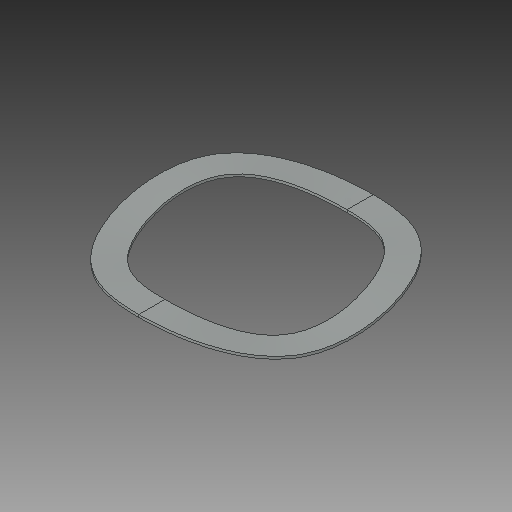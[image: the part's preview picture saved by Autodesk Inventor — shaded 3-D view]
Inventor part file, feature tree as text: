
AUTODESK INVENTOR PART (.ipt)
format: ipt  version: 2018 (Build 220112000, 112)  size: 123,392 bytes
history: native  units: in
note: dims shown in document units (in); Inventor stores cm internally (conversion verified against a paired STEP export)
features: loft x1
ambient origin geometry x8: Origin, YZ Plane, XZ Plane, XY Plane, X Axis, Y Axis, Z Axis, Center Point
bodies: Solid1 (feature_tree)
feature tree (1):
  loft  "Loft1"
